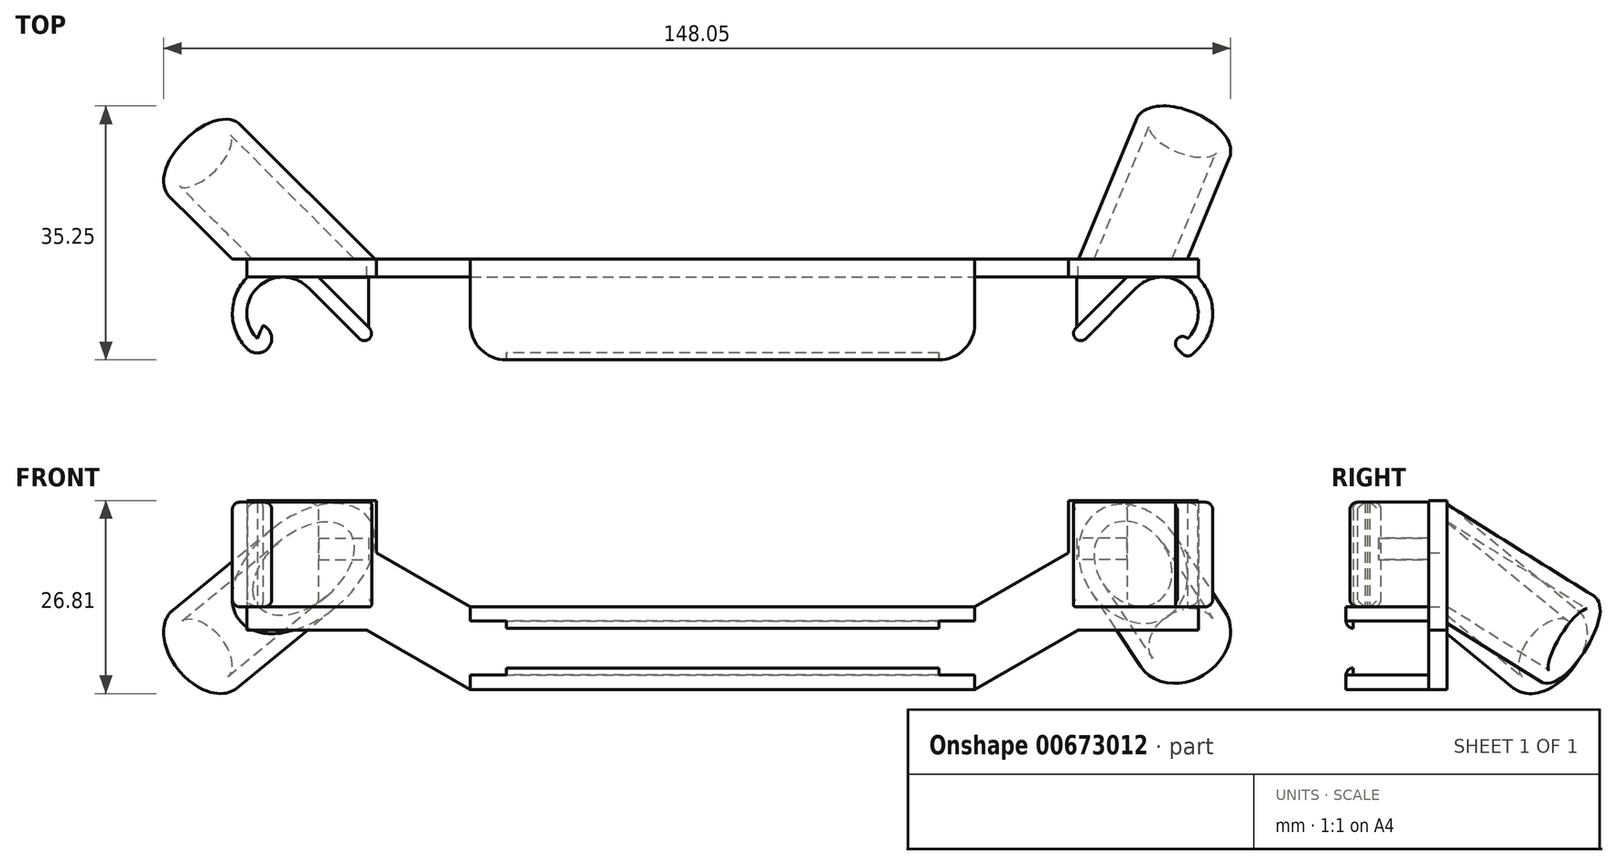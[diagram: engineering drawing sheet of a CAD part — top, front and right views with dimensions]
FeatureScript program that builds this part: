
annotation { "Feature Type Name" : "Feature", "Feature Type Description" : "" }
export const myFeature = defineFeature(function(context is Context, id is Id, definition is map)
    precondition{}
    {
        {
            var Q0;
            Q0=qCreatedBy(makeId("Front.planeOp"),FACE);
            var sketch = newSketch(context, id + "F0", { "sketchPlane" : qUnion([Q0])});
            skLineSegment(sketch, "E0.bottom", {"start": v(-66, 23) * mm, "end": v(-55, 23) * mm});
            skLineSegment(sketch, "E0.left", {"start": v(-66, 23) * mm, "end": v(-66, 11.5) * mm});
            skLineSegment(sketch, "E0.right", {"start": v(66, 23) * mm, "end": v(66, 11.5) * mm});
            skLineSegment(sketch, "E1.bottom", {"start": v(-35, 0) * mm, "end": v(35, 0) * mm});
            skLineSegment(sketch, "E1.top", {"start": v(-35, 11.5) * mm, "end": v(35, 11.5) * mm});
            skLineSegment(sketch, "E1.left", {"start": v(-35, 0) * mm, "end": v(-35, 11.5) * mm});
            skLineSegment(sketch, "E1.right", {"start": v(35, 0) * mm, "end": v(35, 11.5) * mm});
            skLineSegment(sketch, "E2", {"start": v(-35, 9.5) * mm, "end": v(35, 9.5) * mm});
            skLineSegment(sketch, "E3", {"start": v(-35, 2) * mm, "end": v(35, 2) * mm});
            skLineSegment(sketch, "E4", {"start": v(-35, 11.5) * mm, "end": v(-55, 23) * mm});
            skLineSegment(sketch, "E5", {"start": v(-66, 11.5) * mm, "end": v(-55, 11.5) * mm});
            skLineSegment(sketch, "E6", {"start": v(55, 11.5) * mm, "end": v(66, 11.5) * mm});
            skLineSegment(sketch, "E7", {"start": v(35, 11.5) * mm, "end": v(55, 23) * mm});
            skLineSegment(sketch, "E8", {"start": v(35, 0) * mm, "end": v(55, 11.5) * mm});
            skLineSegment(sketch, "E9", {"start": v(-35, 0) * mm, "end": v(-55, 11.5) * mm});
            skLineSegment(sketch, "E10.trimOffspring", {"start": v(55, 23) * mm, "end": v(66, 23) * mm});
            skPoint(sketch, "E11.trimOffspring.start.orphan", {"position": v(55, 0) * mm});
            skPoint(sketch, "E0.top.end.orphan", {"position": v(-55, 0) * mm});
            skPoint(sketch, "E12.start.orphan", {"position": v(-66, 0) * mm});
            skPoint(sketch, "E13.orphan", {"position": v(-75, 0) * mm});
            skPoint(sketch, "E14.end.orphan", {"position": v(66, 0) * mm});
            skPoint(sketch, "E14.start.orphan", {"position": v(75, 0) * mm});
            skLineSegment(sketch, "E15", {"start": v(66, 8.25) * mm, "end": v(66, 26.25) * mm});
            skLineSegment(sketch, "E16", {"start": v(66, 26.25) * mm, "end": v(48, 26.25) * mm});
            skLineSegment(sketch, "E17", {"start": v(48, 26.25) * mm, "end": v(48, 8.25) * mm});
            skLineSegment(sketch, "E18", {"start": v(48, 8.25) * mm, "end": v(66, 8.25) * mm});
            skLineSegment(sketch, "E19", {"start": v(-66, 26.25) * mm, "end": v(-66, 8.25) * mm});
            skLineSegment(sketch, "E20", {"start": v(-66, 8.25) * mm, "end": v(-48, 8.25) * mm});
            skLineSegment(sketch, "E21", {"start": v(-48, 8.25) * mm, "end": v(-48, 26.25) * mm});
            skLineSegment(sketch, "E22", {"start": v(-48, 26.25) * mm, "end": v(-66, 26.25) * mm});
            skSolve(sketch);
        }
        {
            var Q0;
            Q0=makeQuery(id+"F0.imprint","IMPRINT",FACE,{"disambiguationData":[TD([[makeQuery(id+"F0.imprint","IMPRINT",EDGE,{"derivedFrom":sQuery(id+"F0.wireOp",EDGE,"E0.bottom")}),-1.0]])]});
            var Q1;
            Q1=makeQuery(id+"F0.imprint","IMPRINT",FACE,{"disambiguationData":[TD([[makeQuery(id+"F0.imprint","IMPRINT",EDGE,{"derivedFrom":sQuery(id+"F0.wireOp",EDGE,"E0.right")}),-1.0]])]});
            var Q2;
            {var subQ0=sQuery(id+"F0.wireOp",EDGE,"E2");Q2=makeQuery(id+"F0.imprint","IMPRINT",FACE,{"disambiguationData":[TD([[makeQuery(id+"F0.imprint","IMPRINT",EDGE,{"derivedFrom":subQ0}),-1.0]])]});}
            var Q3;
            {var subQ1=sQuery(id+"F0.wireOp",EDGE,"E1.right");var subQ5=makeQuery(id+"F0.imprint","INTERSECT",VERTEX,{"derivedFrom":[subQ1,sQuery(id+"F0.wireOp",EDGE,"E2")]});Q3=makeQuery(id+"F0.imprint","IMPRINT",FACE,{"disambiguationData":[TD([[makeQuery(id+"F0.imprint","IMPRINT",EDGE,{"disambiguationData":[TD([[subQ5,1.0]])],"derivedFrom":subQ1}),-1.0]])]});}
            var Q4;
            {var subQ2=sQuery(id+"F0.wireOp",EDGE,"E6");Q4=makeQuery(id+"F0.imprint","IMPRINT",FACE,{"disambiguationData":[TD([[makeQuery(id+"F0.imprint","IMPRINT",EDGE,{"derivedFrom":subQ2}),1.0]])]});}
            var Q5;
            {var subQ0=sQuery(id+"F0.wireOp",EDGE,"E6");Q5=makeQuery(id+"F0.imprint","IMPRINT",FACE,{"disambiguationData":[TD([[makeQuery(id+"F0.imprint","IMPRINT",EDGE,{"derivedFrom":subQ0}),-1.0]])]});}
            var Q6;
            {var subQ1=sQuery(id+"F0.wireOp",EDGE,"E10.trimOffspring");Q6=makeQuery(id+"F0.imprint","IMPRINT",FACE,{"disambiguationData":[TD([[makeQuery(id+"F0.imprint","IMPRINT",EDGE,{"derivedFrom":subQ1}),1.0]])]});}
            var Q7;
            {var subQ1=sQuery(id+"F0.wireOp",EDGE,"E1.left");var subQ5=makeQuery(id+"F0.imprint","INTERSECT",VERTEX,{"derivedFrom":[subQ1,sQuery(id+"F0.wireOp",EDGE,"E2")]});Q7=makeQuery(id+"F0.imprint","IMPRINT",FACE,{"disambiguationData":[TD([[makeQuery(id+"F0.imprint","IMPRINT",EDGE,{"disambiguationData":[TD([[subQ5,1.0]])],"derivedFrom":subQ1}),1.0]])]});}
            var Q8;
            {var subQ0=sQuery(id+"F0.wireOp",EDGE,"E5");Q8=makeQuery(id+"F0.imprint","IMPRINT",FACE,{"disambiguationData":[TD([[makeQuery(id+"F0.imprint","IMPRINT",EDGE,{"derivedFrom":subQ0}),-1.0]])]});}
            var Q9;
            {var subQ4=sQuery(id+"F0.wireOp",EDGE,"E0.bottom");Q9=makeQuery(id+"F0.imprint","IMPRINT",FACE,{"disambiguationData":[TD([[makeQuery(id+"F0.imprint","IMPRINT",EDGE,{"derivedFrom":subQ4}),1.0]])]});}
            extrude(context, id + "F1", {"entities" : qUnion([Q0, Q1, Q2, Q3, Q4, Q5, Q6, Q7, Q8, Q9]), "depth" : 2.5 * mm, "offsetDistance" : 2.5 * mm});
        }
        {
            var Q0;
            {var subQ0=sQuery(id+"F0.wireOp",EDGE,"E1.top");Q0=makeQuery(id+"F0.imprint","IMPRINT",FACE,{"disambiguationData":[TD([[makeQuery(id+"F0.imprint","IMPRINT",EDGE,{"derivedFrom":subQ0}),-1.0]])]});}
            var Q1;
            {var subQ2=sQuery(id+"F0.wireOp",EDGE,"E3");Q1=makeQuery(id+"F0.imprint","IMPRINT",FACE,{"disambiguationData":[TD([[makeQuery(id+"F0.imprint","IMPRINT",EDGE,{"derivedFrom":subQ2}),-1.0]])]});}
            extrude(context, id + "F2", {"entities" : qUnion([Q0, Q1]), "operationType" : NewBodyOperationType.ADD, "depth" : 14 * mm, "offsetDistance" : 25 * mm});
        }
        {
            var Q0;
            Q0=qCreatedBy(makeId("Right.planeOp"),FACE);
            var sketch = newSketch(context, id + "F3", { "sketchPlane" : qUnion([Q0])});
            skArc(sketch, "E23", {"start": v(-14, 9.5) * mm, "mid": v(-13.7, 8.8) * mm, "end": v(-13, 8.5) * mm});
            skLineSegment(sketch, "E24", {"start": v(-13, 9.5) * mm, "end": v(-13, 8.5) * mm});
            skLineSegment(sketch, "E25", {"start": v(-13, 9.5) * mm, "end": v(-14, 9.5) * mm});
            skArc(sketch, "E26", {"start": v(-13, 3) * mm, "mid": v(-13.7, 2.7) * mm, "end": v(-14, 2) * mm});
            skLineSegment(sketch, "E27", {"start": v(-13, 3) * mm, "end": v(-13, 2) * mm});
            skLineSegment(sketch, "E28", {"start": v(-13, 2) * mm, "end": v(-14, 2) * mm});
            skSolve(sketch);
        }
        {
            var Q0;
            Q0=makeQuery(id+"F3.imprint","IMPRINT",FACE,{"disambiguationData":[TD([[makeQuery(id+"F3.imprint","IMPRINT",EDGE,{"derivedFrom":sQuery(id+"F3.wireOp",EDGE,"E23")}),1.0]])]});
            var Q1;
            Q1=makeQuery(id+"F3.imprint","IMPRINT",FACE,{"disambiguationData":[TD([[makeQuery(id+"F3.imprint","IMPRINT",EDGE,{"derivedFrom":sQuery(id+"F3.wireOp",EDGE,"E26")}),1.0]])]});
            extrude(context, id + "F4", {"entities" : qUnion([Q0, Q1]), "operationType" : NewBodyOperationType.ADD, "endBound" : BoundingType.SYMMETRIC, "depth" : 60 * mm, "offsetDistance" : 25 * mm});
        }
        {
            var Q0;
            {var subQ0=sQuery(id+"F0.wireOp",EDGE,"E1.right");Q0=makeQuery(id+"F2.opExtrude","CAP_EDGE",EDGE,{"disambiguationData":[OSD([subQ0]),TDD([makeQuery(id+"F0.imprint","IMPRINT",EDGE,{"disambiguationData":[TD([[makeQuery(id+"F0.imprint","INTERSECT",VERTEX,{"derivedFrom":[subQ0,sQuery(id+"F0.wireOp",EDGE,"E2")]}),-1.0]])],"derivedFrom":subQ0})])],"isStart":false});}
            var Q1;
            {var subQ0=sQuery(id+"F0.wireOp",EDGE,"E1.right");Q1=makeQuery(id+"F2.opExtrude","CAP_EDGE",EDGE,{"disambiguationData":[OSD([subQ0]),TDD([makeQuery(id+"F0.imprint","IMPRINT",EDGE,{"disambiguationData":[TD([[makeQuery(id+"F0.imprint","INTERSECT",VERTEX,{"derivedFrom":[subQ0,sQuery(id+"F0.wireOp",EDGE,"E3")]}),1.0]])],"derivedFrom":subQ0})])],"isStart":false});}
            var Q2;
            {var subQ0=sQuery(id+"F0.wireOp",EDGE,"E1.left");Q2=makeQuery(id+"F2.opExtrude","CAP_EDGE",EDGE,{"disambiguationData":[OSD([subQ0]),TDD([makeQuery(id+"F0.imprint","IMPRINT",EDGE,{"disambiguationData":[TD([[makeQuery(id+"F0.imprint","INTERSECT",VERTEX,{"derivedFrom":[subQ0,sQuery(id+"F0.wireOp",EDGE,"E3")]}),1.0]])],"derivedFrom":subQ0})])],"isStart":false});}
            var Q3;
            {var subQ0=sQuery(id+"F0.wireOp",EDGE,"E1.left");Q3=makeQuery(id+"F2.opExtrude","CAP_EDGE",EDGE,{"disambiguationData":[OSD([subQ0]),TDD([makeQuery(id+"F0.imprint","IMPRINT",EDGE,{"disambiguationData":[TD([[makeQuery(id+"F0.imprint","INTERSECT",VERTEX,{"derivedFrom":[subQ0,sQuery(id+"F0.wireOp",EDGE,"E2")]}),-1.0]])],"derivedFrom":subQ0})])],"isStart":false});}
            fillet(context, id + "F5", {"entities" : qUnion([Q0, Q1, Q2, Q3]), "radius" : 5 * mm, "tangentPropagation" : true, "allowEdgeOverflow" : false});
        }
        {
            var Q0;
            Q0=qCreatedBy(makeId("Top.planeOp"),FACE);
            var sketch = newSketch(context, id + "F6", { "sketchPlane" : qUnion([Q0])});
            skArc(sketch, "E29", {"start": v(64.54, -11.04) * mm, "mid": v(64.54, -3.96) * mm, "end": v(57.46, -3.96) * mm});
            skArc(sketch, "E30", {"start": v(65.95, -12.45) * mm, "mid": v(65.95, -2.55) * mm, "end": v(56.05, -2.55) * mm});
            skLineSegment(sketch, "E31", {"start": v(56.05, -2.55) * mm, "end": v(48.27, -10.33) * mm});
            skLineSegment(sketch, "E32", {"start": v(57.46, -3.96) * mm, "end": v(49.69, -11.74) * mm});
            skLineSegment(sketch, "E33", {"start": v(48.27, -10.33) * mm, "end": v(49.69, -11.74) * mm});
            skLineSegment(sketch, "E34.0", {"start": v(48.27, -10.33) * mm, "end": v(48.27, -10.33) * mm});
            skLineSegment(sketch, "E34.1", {"start": v(48.27, -10.33) * mm, "end": v(56.05, -2.55) * mm, "construction": true});
            skLineSegment(sketch, "E35.0", {"start": v(61, -7.5) * mm, "end": v(64.54, -11.04) * mm, "construction": true});
            skArc(sketch, "E36", {"start": v(-57.46, -3.96) * mm, "mid": v(-64.54, -3.96) * mm, "end": v(-64.54, -11.04) * mm});
            skArc(sketch, "E37", {"start": v(-56.05, -2.55) * mm, "mid": v(-65.95, -2.55) * mm, "end": v(-65.95, -12.45) * mm});
            skLineSegment(sketch, "E38", {"start": v(-57.46, -3.96) * mm, "end": v(-49.69, -11.74) * mm});
            skLineSegment(sketch, "E39", {"start": v(-56.05, -2.55) * mm, "end": v(-48.27, -10.33) * mm});
            skLineSegment(sketch, "E40", {"start": v(-49.69, -11.74) * mm, "end": v(-48.27, -10.33) * mm});
            skLineSegment(sketch, "E41.0", {"start": v(-48.27, -10.33) * mm, "end": v(-48.27, -10.33) * mm});
            skLineSegment(sketch, "E41.1", {"start": v(-48.27, -10.33) * mm, "end": v(-56.05, -2.55) * mm, "construction": true});
            skLineSegment(sketch, "E42.0", {"start": v(-61, -7.5) * mm, "end": v(-57.46, -3.96) * mm, "construction": true});
            skLineSegment(sketch, "E43", {"start": v(-66, -2.5) * mm, "end": v(-66, -2.6) * mm});
            skLineSegment(sketch, "E44", {"start": v(66, -2.5) * mm, "end": v(66, -2.6) * mm});
            skArc(sketch, "E45", {"start": v(-65.95, -12.45) * mm, "mid": v(-62.88, -12.16) * mm, "end": v(-63.75, -9.2) * mm});
            skLineSegment(sketch, "E46", {"start": v(-64.54, -11.04) * mm, "end": v(-63.75, -9.2) * mm});
            skPoint(sketch, "E47.orphan", {"position": v(-62.54, -11.04) * mm});
            skLineSegment(sketch, "E48", {"start": v(64.54, -11.04) * mm, "end": v(64.53, -11.04) * mm});
            skLineSegment(sketch, "E49", {"start": v(63.12, -12.45) * mm, "end": v(64.54, -13.87) * mm});
            skLineSegment(sketch, "E50", {"start": v(64.54, -13.87) * mm, "end": v(65.95, -12.45) * mm});
            skArc(sketch, "E51", {"start": v(64.53, -11.04) * mm, "mid": v(63.12, -11.04) * mm, "end": v(63.12, -12.45) * mm});
            skLineSegment(sketch, "E52.trimOffspring", {"start": v(63.12, -12.45) * mm, "end": v(63.12, -12.45) * mm});
            skLineSegment(sketch, "E53", {"start": v(-66.13, 0.05) * mm, "end": v(-48.44, 17.74) * mm});
            skLineSegment(sketch, "E54", {"start": v(-49.1, -2.55) * mm, "end": v(-49.1, -9.5) * mm});
            skLineSegment(sketch, "E55", {"start": v(-49.1, -2.55) * mm, "end": v(-56.05, -2.55) * mm});
            skLineSegment(sketch, "E56", {"start": v(49.16, -9.45) * mm, "end": v(49.16, -2.56) * mm});
            skLineSegment(sketch, "E57", {"start": v(49.16, -2.56) * mm, "end": v(56.05, -2.55) * mm});
            skSolve(sketch);
        }
        {
            var Q0;
            Q0=makeQuery(id+"F6.imprint","IMPRINT",FACE,{"disambiguationData":[TD([[makeQuery(id+"F6.imprint","IMPRINT",EDGE,{"derivedFrom":sQuery(id+"F6.wireOp",EDGE,"E36")}),-1.0]])]});
            var Q1;
            Q1=makeQuery(id+"F6.imprint","IMPRINT",FACE,{"disambiguationData":[TD([[makeQuery(id+"F6.imprint","IMPRINT",EDGE,{"derivedFrom":sQuery(id+"F6.wireOp",EDGE,"E29")}),-1.0]])]});
            extrude(context, id + "F7", {"entities" : qUnion([Q0, Q1]), "operationType" : NewBodyOperationType.ADD, "depth" : 26 * mm, "offsetDistance" : 25 * mm, "hasSecondDirection" : true, "secondDirectionOppositeDirection" : false, "secondDirectionDepth" : 11.5 * mm});
        }
        {
            var Q0;
            Q0=qCreatedBy(makeId("Top.planeOp"),FACE);
            var sketch = newSketch(context, id + "F8", { "sketchPlane" : qUnion([Q0])});
            skLineSegment(sketch, "E58", {"start": v(55.98, 4.25) * mm, "end": v(66, 0.1) * mm});
            skSolve(sketch);
        }
        {
            var Q0;
            Q0=sQuery(id+"F8.wireOp",EDGE,"E58");
            cPlane(context, id + "F9", {"entities" : qUnion([Q0]), "cplaneType" : CPlaneType.LINE_ANGLE, "offset" : 25 * mm, "angle" : 30 * degree, "oppositeDirection" : true, "width" : 150 * mm, "height" : 150 * mm});
        }
        {
            var Q0;
            Q0=qCreatedBy(id+"F9.planeOp",FACE);
            var sketch = newSketch(context, id + "F10", { "sketchPlane" : qUnion([Q0])});
            skCircle(sketch, "E59", {"center": v(-56.8, 14.8) * mm, "radius": 7 * mm});
            skCircle(sketch, "E60", {"center": v(-56.8, 14.8) * mm, "radius": 5 * mm});
            skSolve(sketch);
        }
        {
            var Q0;
            Q0=makeQuery(id+"F10.imprint","IMPRINT",FACE,{"disambiguationData":[TD([[makeQuery(id+"F10.imprint","IMPRINT",EDGE,{"derivedFrom":sQuery(id+"F10.wireOp",EDGE,"E59")}),1.0]])]});
            var Q1;
            {var subQ0=sQuery(id+"F0.wireOp",EDGE,"E3");var subQ1=sQuery(id+"F0.wireOp",EDGE,"E1.right");var subQ2=sQuery(id+"F0.wireOp",EDGE,"E1.left");var subQ3=sQuery(id+"F0.wireOp",EDGE,"E2");Q1=makeQuery(id+"F2.boolean.opBoolean","MERGE",FACE,{"derivedFrom":[makeQuery(id+"F1.opExtrude","CAP_FACE",FACE,{"disambiguationData":[OSD([sQuery(id+"F0.wireOp",EDGE,"E0.bottom"),sQuery(id+"F0.wireOp",EDGE,"E0.left"),subQ2,subQ1,subQ3,subQ0,sQuery(id+"F0.wireOp",EDGE,"E4"),sQuery(id+"F0.wireOp",EDGE,"E5"),sQuery(id+"F0.wireOp",EDGE,"E7"),sQuery(id+"F0.wireOp",EDGE,"E8"),sQuery(id+"F0.wireOp",EDGE,"E9"),sQuery(id+"F0.wireOp",EDGE,"E15"),sQuery(id+"F0.wireOp",EDGE,"E16"),sQuery(id+"F0.wireOp",EDGE,"E17"),sQuery(id+"F0.wireOp",EDGE,"E18")])],"isStart":true}),makeQuery(id+"F2.opExtrude","CAP_FACE",FACE,{"disambiguationData":[OSD([sQuery(id+"F0.wireOp",EDGE,"E1.top"),subQ2,subQ1,subQ3])],"isStart":true}),makeQuery(id+"F2.opExtrude","CAP_FACE",FACE,{"disambiguationData":[OSD([subQ2,subQ1,subQ0,sQuery(id+"F0.wireOp",EDGE,"E1.bottom")])],"isStart":true})]});}
            var Q2;
            Q2=makeQuery(id+"F1.opExtrude","SWEPT_BODY",BODY,{"disambiguationData":[OSD([sQuery(id+"F0.wireOp",EDGE,"E0.bottom"),sQuery(id+"F0.wireOp",EDGE,"E0.left"),sQuery(id+"F0.wireOp",EDGE,"E0.right"),sQuery(id+"F0.wireOp",EDGE,"E1.left"),sQuery(id+"F0.wireOp",EDGE,"E1.right"),sQuery(id+"F0.wireOp",EDGE,"E2"),sQuery(id+"F0.wireOp",EDGE,"E3"),sQuery(id+"F0.wireOp",EDGE,"E4"),sQuery(id+"F0.wireOp",EDGE,"E5"),sQuery(id+"F0.wireOp",EDGE,"E6"),sQuery(id+"F0.wireOp",EDGE,"E7"),sQuery(id+"F0.wireOp",EDGE,"E8"),sQuery(id+"F0.wireOp",EDGE,"E9"),sQuery(id+"F0.wireOp",EDGE,"E10.trimOffspring")])]});
            var Q3;
            Q3=makeQuery(id+"F1.opExtrude","SWEPT_BODY",BODY,{"disambiguationData":[OSD([sQuery(id+"F0.wireOp",EDGE,"E0.bottom"),sQuery(id+"F0.wireOp",EDGE,"E0.left"),sQuery(id+"F0.wireOp",EDGE,"E0.right"),sQuery(id+"F0.wireOp",EDGE,"E1.left"),sQuery(id+"F0.wireOp",EDGE,"E1.right"),sQuery(id+"F0.wireOp",EDGE,"E2"),sQuery(id+"F0.wireOp",EDGE,"E3"),sQuery(id+"F0.wireOp",EDGE,"E4"),sQuery(id+"F0.wireOp",EDGE,"E5"),sQuery(id+"F0.wireOp",EDGE,"E6"),sQuery(id+"F0.wireOp",EDGE,"E7"),sQuery(id+"F0.wireOp",EDGE,"E8"),sQuery(id+"F0.wireOp",EDGE,"E9"),sQuery(id+"F0.wireOp",EDGE,"E10.trimOffspring")])]});
            extrude(context, id + "F11", {"entities" : qUnion([Q0]), "operationType" : NewBodyOperationType.ADD, "endBound" : BoundingType.UP_TO_SURFACE, "oppositeDirection" : true, "depth" : 25 * mm, "endBoundEntityFace" : qUnion([Q1]), "endBoundEntityBody" : qUnion([Q2]), "offsetDistance" : 25 * mm, "hasSecondDirection" : true, "secondDirectionOppositeDirection" : false, "secondDirectionDepth" : 10 * mm, "secondDirectionBoundEntityBody" : qUnion([Q3])});
        }
        {
            var Q0;
            Q0=sQuery(id+"F6.wireOp",EDGE,"E53");
            cPlane(context, id + "F12", {"entities" : qUnion([Q0]), "cplaneType" : CPlaneType.LINE_ANGLE, "offset" : 25 * mm, "angle" : 120 * degree, "oppositeDirection" : true, "width" : 150 * mm, "height" : 150 * mm});
        }
        {
            var Q0;
            Q0=qCreatedBy(id+"F12.planeOp",FACE);
            var sketch = newSketch(context, id + "F13", { "sketchPlane" : qUnion([Q0])});
            skCircle(sketch, "E61", {"center": v(52.46, 13) * mm, "radius": 5 * mm});
            skCircle(sketch, "E62", {"center": v(52.46, 13) * mm, "radius": 7 * mm});
            skSolve(sketch);
        }
        {
            var Q0;
            Q0=makeQuery(id+"F13.imprint","IMPRINT",FACE,{"disambiguationData":[TD([[makeQuery(id+"F13.imprint","IMPRINT",EDGE,{"derivedFrom":sQuery(id+"F13.wireOp",EDGE,"E61")}),-1.0]])]});
            var Q1;
            {var subQ0=sQuery(id+"F0.wireOp",EDGE,"E20");var subQ1=sQuery(id+"F0.wireOp",EDGE,"E19");var subQ2=sQuery(id+"F0.wireOp",EDGE,"E18");var subQ3=sQuery(id+"F0.wireOp",EDGE,"E17");var subQ4=sQuery(id+"F0.wireOp",EDGE,"E16");var subQ5=sQuery(id+"F0.wireOp",EDGE,"E15");var subQ6=sQuery(id+"F0.wireOp",EDGE,"E4");var subQ7=sQuery(id+"F0.wireOp",EDGE,"E7");var subQ8=sQuery(id+"F0.wireOp",EDGE,"E1.top");var subQ9=sQuery(id+"F0.wireOp",EDGE,"E8");var subQ10=sQuery(id+"F0.wireOp",EDGE,"E9");var subQ11=sQuery(id+"F0.wireOp",EDGE,"E21");var subQ12=sQuery(id+"F0.wireOp",EDGE,"E22");var subQ13=sQuery(id+"F0.wireOp",EDGE,"E1.bottom");var subQ14=sQuery(id+"F0.wireOp",EDGE,"E3");var subQ15=sQuery(id+"F0.wireOp",EDGE,"E1.right");var subQ16=sQuery(id+"F0.wireOp",EDGE,"E1.left");var subQ17=sQuery(id+"F0.wireOp",EDGE,"E2");Q1=makeQuery(id+"F11.boolean.opBoolean","SPLIT",FACE,{"disambiguationData":[TD([makeQuery(id+"F1.opExtrude","SWEPT_FACE",FACE,{"disambiguationData":[OSD([subQ6])]})])],"derivedFrom":makeQuery(id+"F2.boolean.opBoolean","MERGE",FACE,{"derivedFrom":[makeQuery(id+"F1.opExtrude","CAP_FACE",FACE,{"disambiguationData":[OSD([subQ16,subQ15,subQ17,subQ14,subQ6,subQ7,subQ9,subQ10,subQ5,subQ4,subQ3,subQ2,subQ1,subQ0,subQ11,subQ12])],"isStart":true}),makeQuery(id+"F2.opExtrude","CAP_FACE",FACE,{"disambiguationData":[OSD([subQ8,subQ16,subQ15,subQ17])],"isStart":true}),makeQuery(id+"F2.opExtrude","CAP_FACE",FACE,{"disambiguationData":[OSD([subQ16,subQ15,subQ14,subQ13])],"isStart":true})]})});}
            extrude(context, id + "F14", {"entities" : qUnion([Q0]), "operationType" : NewBodyOperationType.ADD, "endBound" : BoundingType.UP_TO_SURFACE, "oppositeDirection" : true, "depth" : 25 * mm, "endBoundEntityFace" : qUnion([Q1]), "offsetDistance" : 25 * mm, "hasSecondDirection" : true, "secondDirectionOppositeDirection" : false, "secondDirectionDepth" : 10 * mm});
        }
        {
            var Q0;
            {var subQ2=sQuery(id+"F6.wireOp",EDGE,"E54");Q0=makeQuery(id+"F6.imprint","IMPRINT",FACE,{"disambiguationData":[TD([[makeQuery(id+"F6.imprint","IMPRINT",EDGE,{"derivedFrom":subQ2}),-1.0]])]});}
            extrude(context, id + "F15", {"entities" : qUnion([Q0]), "operationType" : NewBodyOperationType.ADD, "depth" : 21 * mm, "offsetDistance" : 25 * mm, "hasSecondDirection" : true, "secondDirectionOppositeDirection" : false, "secondDirectionDepth" : 18 * mm});
        }
        {
            var Q0;
            {var subQ2=sQuery(id+"F6.wireOp",EDGE,"E56");Q0=makeQuery(id+"F6.imprint","IMPRINT",FACE,{"disambiguationData":[TD([[makeQuery(id+"F6.imprint","IMPRINT",EDGE,{"derivedFrom":subQ2}),-1.0]])]});}
            extrude(context, id + "F16", {"entities" : qUnion([Q0]), "operationType" : NewBodyOperationType.ADD, "depth" : 21 * mm, "offsetDistance" : 25 * mm, "hasSecondDirection" : true, "secondDirectionOppositeDirection" : false, "secondDirectionDepth" : 18 * mm});
        }
        {
            var Q0;
            Q0=makeQuery(id+"F14.opExtrude","CAP_EDGE",EDGE,{"disambiguationData":[OSD([sQuery(id+"F13.wireOp",EDGE,"E62")])],"isStart":true});
            var Q1;
            Q1=makeQuery(id+"F14.opExtrude","CAP_EDGE",EDGE,{"disambiguationData":[OSD([sQuery(id+"F13.wireOp",EDGE,"E61")])],"isStart":true});
            var Q2;
            Q2=makeQuery(id+"F11.opExtrude","CAP_EDGE",EDGE,{"disambiguationData":[OSD([sQuery(id+"F10.wireOp",EDGE,"E60")])],"isStart":true});
            var Q3;
            Q3=makeQuery(id+"F11.opExtrude","CAP_EDGE",EDGE,{"disambiguationData":[OSD([sQuery(id+"F10.wireOp",EDGE,"E59")])],"isStart":true});
            var Q4;
            Q4=makeQuery(id+"F16.opExtrude","CAP_EDGE",EDGE,{"disambiguationData":[OSD([sQuery(id+"F6.wireOp",EDGE,"E31")])],"isStart":false});
            var Q5;
            Q5=makeQuery(id+"F16.opExtrude","CAP_EDGE",EDGE,{"disambiguationData":[OSD([sQuery(id+"F6.wireOp",EDGE,"E31")])],"isStart":true});
            var Q6;
            Q6=makeQuery(id+"F7.opExtrude","CAP_EDGE",EDGE,{"disambiguationData":[OSD([sQuery(id+"F6.wireOp",EDGE,"E31")])],"isStart":false});
            var Q7;
            Q7=makeQuery(id+"F7.opExtrude","SWEPT_EDGE",EDGE,{"disambiguationData":[OSD([sQuery(id+"F6.wireOp",EDGE,"E31"),sQuery(id+"F6.wireOp",EDGE,"E33")])]});
            var Q8;
            Q8=makeQuery(id+"F7.opExtrude","CAP_EDGE",EDGE,{"disambiguationData":[OSD([sQuery(id+"F6.wireOp",EDGE,"E31")])],"isStart":true});
            var Q9;
            Q9=makeQuery(id+"F7.opExtrude","SWEPT_EDGE",EDGE,{"disambiguationData":[OSD([sQuery(id+"F6.wireOp",EDGE,"E32"),sQuery(id+"F6.wireOp",EDGE,"E33")])]});
            var Q10;
            Q10=makeQuery(id+"F7.opExtrude","SWEPT_EDGE",EDGE,{"disambiguationData":[OSD([sQuery(id+"F6.wireOp",EDGE,"E49"),sQuery(id+"F6.wireOp",EDGE,"E50")])]});
            var Q11;
            {var subQ0=sQuery(id+"F6.wireOp",EDGE,"E50");var subQ1=sQuery(id+"F6.wireOp",EDGE,"E30");Q11=makeQuery(id+"F7.boolean.opBoolean","SPLIT",EDGE,{"disambiguationData":[TD([makeQuery(id+"F7.opExtrude","SWEPT_FACE",FACE,{"disambiguationData":[OSD([subQ0])]})])],"derivedFrom":makeQuery(id+"F7.opExtrude","CAP_EDGE",EDGE,{"disambiguationData":[OSD([subQ1])],"isStart":false})});}
            var Q12;
            {var subQ0=sQuery(id+"F6.wireOp",EDGE,"E50");var subQ1=sQuery(id+"F6.wireOp",EDGE,"E30");Q12=makeQuery(id+"F7.boolean.opBoolean","SPLIT",EDGE,{"disambiguationData":[TD([makeQuery(id+"F7.opExtrude","SWEPT_FACE",FACE,{"disambiguationData":[OSD([subQ0])]})])],"derivedFrom":makeQuery(id+"F7.opExtrude","CAP_EDGE",EDGE,{"disambiguationData":[OSD([subQ1])],"isStart":true})});}
            var Q13;
            Q13=makeQuery(id+"F7.opExtrude","CAP_EDGE",EDGE,{"disambiguationData":[OSD([sQuery(id+"F6.wireOp",EDGE,"E49")])],"isStart":true});
            var Q14;
            Q14=makeQuery(id+"F7.opExtrude","CAP_EDGE",EDGE,{"disambiguationData":[OSD([sQuery(id+"F6.wireOp",EDGE,"E50")])],"isStart":true});
            var Q15;
            Q15=makeQuery(id+"F7.opExtrude","CAP_EDGE",EDGE,{"disambiguationData":[OSD([sQuery(id+"F6.wireOp",EDGE,"E50")])],"isStart":false});
            var Q16;
            Q16=makeQuery(id+"F7.opExtrude","CAP_EDGE",EDGE,{"disambiguationData":[OSD([sQuery(id+"F6.wireOp",EDGE,"E49")])],"isStart":false});
            var Q17;
            Q17=makeQuery(id+"F15.opExtrude","CAP_EDGE",EDGE,{"disambiguationData":[OSD([sQuery(id+"F6.wireOp",EDGE,"E39")])],"isStart":false});
            var Q18;
            Q18=makeQuery(id+"F7.opExtrude","SWEPT_EDGE",EDGE,{"disambiguationData":[OSD([sQuery(id+"F6.wireOp",EDGE,"E39"),sQuery(id+"F6.wireOp",EDGE,"E40")])]});
            var Q19;
            Q19=makeQuery(id+"F7.opExtrude","SWEPT_EDGE",EDGE,{"disambiguationData":[OSD([sQuery(id+"F6.wireOp",EDGE,"E38"),sQuery(id+"F6.wireOp",EDGE,"E40")])]});
            var Q20;
            Q20=makeQuery(id+"F7.opExtrude","CAP_EDGE",EDGE,{"disambiguationData":[OSD([sQuery(id+"F6.wireOp",EDGE,"E39")])],"isStart":true});
            var Q21;
            Q21=makeQuery(id+"F15.opExtrude","CAP_EDGE",EDGE,{"disambiguationData":[OSD([sQuery(id+"F6.wireOp",EDGE,"E39")])],"isStart":true});
            var Q22;
            Q22=makeQuery(id+"F7.opExtrude","CAP_EDGE",EDGE,{"disambiguationData":[OSD([sQuery(id+"F6.wireOp",EDGE,"E39")])],"isStart":false});
            var Q23;
            {var subQ0=sQuery(id+"F6.wireOp",EDGE,"E45");var subQ1=sQuery(id+"F6.wireOp",EDGE,"E37");Q23=makeQuery(id+"F7.boolean.opBoolean","SPLIT",EDGE,{"disambiguationData":[TD([makeQuery(id+"F7.opExtrude","SWEPT_FACE",FACE,{"disambiguationData":[OSD([subQ0])]})])],"derivedFrom":makeQuery(id+"F7.opExtrude","CAP_EDGE",EDGE,{"disambiguationData":[OSD([subQ1])],"isStart":false})});}
            var Q24;
            {var subQ0=sQuery(id+"F6.wireOp",EDGE,"E45");var subQ1=sQuery(id+"F6.wireOp",EDGE,"E37");Q24=makeQuery(id+"F7.boolean.opBoolean","SPLIT",EDGE,{"disambiguationData":[TD([makeQuery(id+"F7.opExtrude","SWEPT_FACE",FACE,{"disambiguationData":[OSD([subQ0])]})])],"derivedFrom":makeQuery(id+"F7.opExtrude","CAP_EDGE",EDGE,{"disambiguationData":[OSD([subQ1])],"isStart":true})});}
            fillet(context, id + "F17", {"entities" : qUnion([Q0, Q1, Q2, Q3, Q4, Q5, Q6, Q7, Q8, Q9, Q10, Q11, Q12, Q13, Q14, Q15, Q16, Q17, Q18, Q19, Q20, Q21, Q22, Q23, Q24]), "radius" : 1 * mm, "tangentPropagation" : true, "allowEdgeOverflow" : false});
        }
    });
